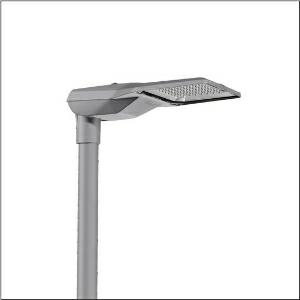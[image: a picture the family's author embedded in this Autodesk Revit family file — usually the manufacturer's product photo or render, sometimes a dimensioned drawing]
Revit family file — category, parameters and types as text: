
# Revit family: streetlight_sl_21_midi___st0_5a_5xe3b43s08lb_de93
name_source: partatom
category: Lighting Fixtures
units: mm (PartAtom-declared; Revit-internal decimal feet)

## family parameters
Cut with Voids When Loaded = No
Host = Face
Light Source = No
Part Type = Normal
Room Calculation Point = No
Round Connector Dimension = Use Diameter
Shared = No

## types (1)
- --- (1 x LED, 14950 lm, 99.6 W, 4000K)
    Apparent Load = 100 VA
    CIE Flux Codes = 41 75 97 100 100
    Color Rendering = 70
    Color Temperature = 4000K
    Default Elevation = 1800 mm
    Description = Streetlight SL 21 midi, mast luminaire, primary light control with lens, of PMMA, primary optical cover: cover, of toughened safety glass, transparent, light distribution: ST0.5a, light emission: direct distribution, primary light characteristic: asymmetric, installation type: side-entry, post-top, LED, High Power LED, rated luminous flux: 14.950lm, luminous efficacy: 150lm/W, light colour: 740, colour temperature: 4000K, control gear: D4i, control: overheat protection, constant luminous flux control, time-dependent luminous flux control, flexible luminous flux parameterisation, pre-setting: logarithmic dimming characteristic, mains connection: 230..240V, AC, 50/60Hz, start of lifetime: 100W, end of service life: 102W, reduction: 46W, luminaire housing, of diecast aluminium, powder-coated, Siteco® metallic grey (DB 702S), corrosivity category C5 mid according to DIN EN ISO 12944, please order mast flange separately, inclination adjustable: 0°, 5°, 10°, 15°, sealing non-destructively replaceable, multi-level sealing system, length: 644mm, width: 335mm, height: 110mm, mast flange for spigot size: 42mm (side-entry): 5XC10008XM4, 60/48mm (side-entry/post-top): 5XC10108XM2, 76/60mm (side-entry/post-top): 5XC10108XM1, mounting height: 4..8m, Smart Interface above, protection rating (complete): IP66, insulation class (complete): insulation class II (safety insulation), certification: CE, ENEC, ENEC+, VDE, impact resistance: IK10, permissible operating ambient temperature for outdoor applications: -40..+50°C, standard-compliant lighting for roads and squares, packaging unit: 1 piece

Light Distribution: ST0.5a
    Height = 111 mm
    Lamp = 1 x LED
    Lamp Light Flux = 14950 lm
    Lamp Power = 99.6 W
    Lamp count = 1
    Length = 644 mm
    Luminous efficacy = 150 lm/W
    Manufacturer = Siteco
    ModVariant = No
    Model = 5XE3B43S08LB
    Number of Poles = 1
    OnlyDefault = Yes
    Power Factor = 1
    Product Name = Streetlight SL 21 midi | ST0.5a
    Product group = mast luminaire | pylon top
    ProductGroupID = 6100
    Protection Class = Protection class II
    Protection Degree = IP 66
    RLX_Detail_Level = 1
    RLX_Emergency_Light_Flux = 0 lm
    RLX_Emergency_Type = 0
    RLX_Emergency_Type_DB = No
    RlxData = <blob elided: 37837 chars, md5=e83eadeb>
    Socket = socket
    Standby Power = 0 W
    System Light Flux = 14950 lm
    System Power = 100 W
    Type Comments = factory setting: luminous flux: 100 % | dim-lin: 254 | 1020 mA
    Type Image = l_1004302.jpg
    URL = http://relux.com
    VarID = @adj_012745
    Voltage = 0 V
    Weight = 0.00 kg
    Width = 336 mm

## geometry (parser evidence)
native form markers: Blend x4, Sweep x9
no freeform markers — native parametric forms only
